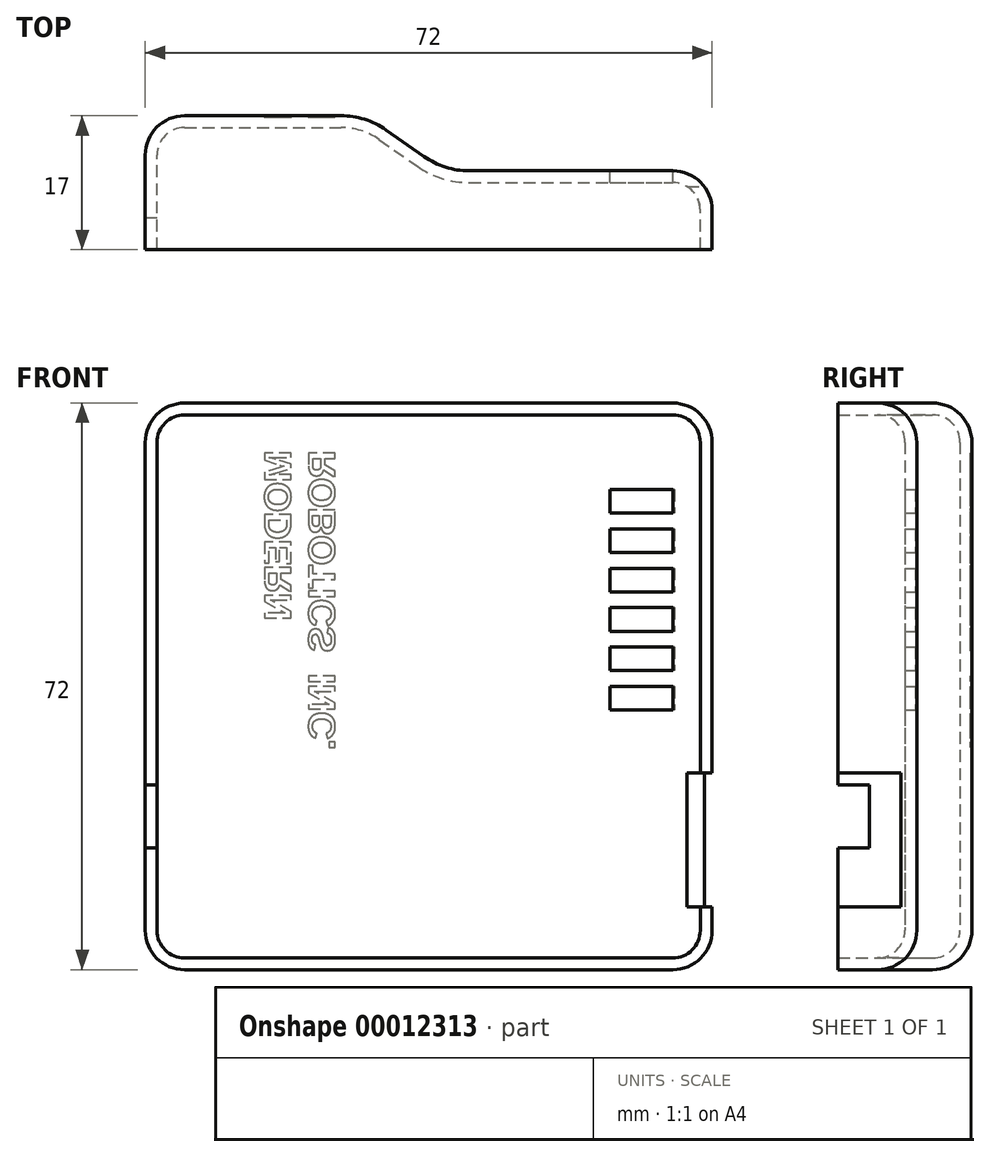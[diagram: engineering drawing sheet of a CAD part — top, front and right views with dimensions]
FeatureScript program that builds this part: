
annotation { "Feature Type Name" : "Feature", "Feature Type Description" : "" }
export const myFeature = defineFeature(function(context is Context, id is Id, definition is map)
    precondition{}
    {
        {
            var Q0;
            Q0=qCreatedBy(makeId("Top.planeOp"),FACE);
            var sketch = newSketch(context, id + "F0", { "sketchPlane" : qUnion([Q0])});
            skPoint(sketch, "E0.visualSharp", {"position": v(28, 17) * mm});
            skPoint(sketch, "E1.visualSharp", {"position": v(38, 10) * mm});
            skLineSegment(sketch, "E2", {"start": v(0, 0) * mm, "end": v(72, 0) * mm});
            skLineSegment(sketch, "E3", {"start": v(72, 10) * mm, "end": v(41.15, 10) * mm});
            skLineSegment(sketch, "E4", {"start": v(72, 0) * mm, "end": v(72, 10) * mm});
            skLineSegment(sketch, "E5", {"start": v(24.85, 17) * mm, "end": v(0, 17) * mm});
            skLineSegment(sketch, "E6", {"start": v(35.42, 11.8) * mm, "end": v(30.58, 15.2) * mm});
            skArc(sketch, "E0.filletArc", {"start": v(30.58, 15.2) * mm, "mid": v(27.85, 16.54) * mm, "end": v(24.85, 17) * mm});
            skLineSegment(sketch, "E7", {"start": v(0, 17) * mm, "end": v(0, 0) * mm});
            skArc(sketch, "E1.filletArc", {"start": v(35.42, 11.8) * mm, "mid": v(38.15, 10.46) * mm, "end": v(41.15, 10) * mm});
            skSolve(sketch);
        }
        {
            var Q0;
            Q0=qSketchRegion(id+"F0",true);
            extrude(context, id + "F1", {"entities" : qUnion([Q0]), "depth" : 72 * mm});
        }
        {
            var Q0;
            Q0=makeQuery(id+"F1.opExtrude","CAP_EDGE",EDGE,{"disambiguationData":[OSD([sQuery(id+"F0.wireOp",EDGE,"E5")])],"isStart":false});
            var Q1;
            Q1=makeQuery(id+"F1.opExtrude","SWEPT_EDGE",EDGE,{"disambiguationData":[OSD([sQuery(id+"F0.wireOp",EDGE,"E3"),sQuery(id+"F0.wireOp",EDGE,"E4")])]});
            var Q2;
            Q2=makeQuery(id+"F1.opExtrude","CAP_EDGE",EDGE,{"disambiguationData":[OSD([sQuery(id+"F0.wireOp",EDGE,"E3")])],"isStart":true});
            var Q3;
            Q3=makeQuery(id+"F1.opExtrude","SWEPT_EDGE",EDGE,{"disambiguationData":[OSD([sQuery(id+"F0.wireOp",EDGE,"E5"),sQuery(id+"F0.wireOp",EDGE,"E7")])]});
            var Q4;
            Q4=makeQuery(id+"F1.opExtrude","CAP_EDGE",EDGE,{"disambiguationData":[OSD([sQuery(id+"F0.wireOp",EDGE,"E7")])],"isStart":false});
            var Q5;
            Q5=makeQuery(id+"F1.opExtrude","CAP_EDGE",EDGE,{"disambiguationData":[OSD([sQuery(id+"F0.wireOp",EDGE,"E4")])],"isStart":false});
            var Q6;
            Q6=makeQuery(id+"F1.opExtrude","CAP_EDGE",EDGE,{"disambiguationData":[OSD([sQuery(id+"F0.wireOp",EDGE,"E4")])],"isStart":true});
            var Q7;
            Q7=makeQuery(id+"F1.opExtrude","CAP_EDGE",EDGE,{"disambiguationData":[OSD([sQuery(id+"F0.wireOp",EDGE,"E7")])],"isStart":true});
            fillet(context, id + "F2", {"entities" : qUnion([Q0, Q1, Q2, Q3, Q4, Q5, Q6, Q7]), "radius" : 5 * mm, "tangentPropagation" : true, "allowEdgeOverflow" : false});
        }
        {
            var Q0;
            Q0=makeQuery(id+"F1.opExtrude","SWEPT_FACE",FACE,{"disambiguationData":[OSD([sQuery(id+"F0.wireOp",EDGE,"E2")])]});
            var Q1;
            Q1=makeQuery(id+"F1.opExtrude","SWEPT_BODY",BODY,{"disambiguationData":[OSD([sQuery(id+"F0.wireOp",EDGE,"E2"),sQuery(id+"F0.wireOp",EDGE,"E3"),sQuery(id+"F0.wireOp",EDGE,"E4"),sQuery(id+"F0.wireOp",EDGE,"E5"),sQuery(id+"F0.wireOp",EDGE,"E6"),sQuery(id+"F0.wireOp",EDGE,"E0.filletArc"),sQuery(id+"F0.wireOp",EDGE,"E7"),sQuery(id+"F0.wireOp",EDGE,"E1.filletArc")])]});
            shell(context, id + "F3", {"entities" : qUnion([Q0]), "parts" : qUnion([Q1]), "thickness" : 1.5 * mm});
        }
        {
            var Q0;
            Q0=makeQuery(id+"F1.opExtrude","SWEPT_FACE",FACE,{"disambiguationData":[OSD([sQuery(id+"F0.wireOp",EDGE,"E7")])]});
            var sketch = newSketch(context, id + "F4", { "sketchPlane" : qUnion([Q0])});
            skLineSegment(sketch, "E8.bottom", {"start": v(0, 23.5) * mm, "end": v(-4, 23.5) * mm});
            skLineSegment(sketch, "E8.top", {"start": v(0, 15.5) * mm, "end": v(-4, 15.5) * mm});
            skLineSegment(sketch, "E8.left", {"start": v(0, 23.5) * mm, "end": v(0, 15.5) * mm});
            skLineSegment(sketch, "E8.right", {"start": v(-4, 23.5) * mm, "end": v(-4, 15.5) * mm});
            skSolve(sketch);
        }
        {
            var Q0;
            Q0=qSketchRegion(id+"F4",true);
            extrude(context, id + "F5", {"entities" : qUnion([Q0]), "operationType" : NewBodyOperationType.REMOVE, "endBound" : BoundingType.UP_TO_NEXT, "oppositeDirection" : true, "depth" : 25 * mm});
        }
        {
            var Q0;
            Q0=makeQuery(id+"F1.opExtrude","SWEPT_FACE",FACE,{"disambiguationData":[OSD([sQuery(id+"F0.wireOp",EDGE,"E5")])]});
            var sketch = newSketch(context, id + "F6", { "sketchPlane" : qUnion([Q0])});
            skText(sketch, "E9", { "text": "MODERN\nROBOTICS  INC.", "fontName": "Arimo-Bold.ttf"});
            const initialGuessF6  = {"E9": [-0.0185, 0.066, 0, -1, 0.0035]};
            skSetInitialGuess(sketch, initialGuessF6);
            skSolve(sketch);
        }
        {
            var Q0;
            Q0=qSketchRegion(id+"F6",true);
            extrude(context, id + "F7", {"entities" : qUnion([Q0]), "operationType" : NewBodyOperationType.REMOVE, "oppositeDirection" : true, "depth" : .2 * mm});
        }
        {
            var Q0;
            Q0=makeQuery(id+"F1.opExtrude","SWEPT_FACE",FACE,{"disambiguationData":[OSD([sQuery(id+"F0.wireOp",EDGE,"E3")])]});
            var sketch = newSketch(context, id + "F8", { "sketchPlane" : qUnion([Q0])});
            skLineSegment(sketch, "E10.bottom", {"start": v(-59, 61) * mm, "end": v(-67, 61) * mm});
            skLineSegment(sketch, "E10.top", {"start": v(-59, 58) * mm, "end": v(-67, 58) * mm});
            skLineSegment(sketch, "E10.left", {"start": v(-59, 61) * mm, "end": v(-59, 58) * mm});
            skLineSegment(sketch, "E10.right", {"start": v(-67, 61) * mm, "end": v(-67, 58) * mm});
            skLineSegment(sketch, "E11.0.1.0", {"start": v(-59, 56) * mm, "end": v(-67, 56) * mm});
            skLineSegment(sketch, "E11.0.1.1", {"start": v(-59, 53) * mm, "end": v(-67, 53) * mm});
            skLineSegment(sketch, "E11.0.1.2", {"start": v(-59, 56) * mm, "end": v(-59, 53) * mm});
            skLineSegment(sketch, "E11.0.1.3", {"start": v(-67, 56) * mm, "end": v(-67, 53) * mm});
            skLineSegment(sketch, "E11.0.2.0", {"start": v(-59, 51) * mm, "end": v(-67, 51) * mm});
            skLineSegment(sketch, "E11.0.2.1", {"start": v(-59, 48) * mm, "end": v(-67, 48) * mm});
            skLineSegment(sketch, "E11.0.2.2", {"start": v(-59, 51) * mm, "end": v(-59, 48) * mm});
            skLineSegment(sketch, "E11.0.2.3", {"start": v(-67, 51) * mm, "end": v(-67, 48) * mm});
            skLineSegment(sketch, "E11.0.3.0", {"start": v(-59, 46) * mm, "end": v(-67, 46) * mm});
            skLineSegment(sketch, "E11.0.3.1", {"start": v(-59, 43) * mm, "end": v(-67, 43) * mm});
            skLineSegment(sketch, "E11.0.3.2", {"start": v(-59, 46) * mm, "end": v(-59, 43) * mm});
            skLineSegment(sketch, "E11.0.3.3", {"start": v(-67, 46) * mm, "end": v(-67, 43) * mm});
            skLineSegment(sketch, "E11.0.4.0", {"start": v(-59, 41) * mm, "end": v(-67, 41) * mm});
            skLineSegment(sketch, "E11.0.4.1", {"start": v(-59, 38) * mm, "end": v(-67, 38) * mm});
            skLineSegment(sketch, "E11.0.4.2", {"start": v(-59, 41) * mm, "end": v(-59, 38) * mm});
            skLineSegment(sketch, "E11.0.4.3", {"start": v(-67, 41) * mm, "end": v(-67, 38) * mm});
            skLineSegment(sketch, "E11.0.5.0", {"start": v(-59, 36) * mm, "end": v(-67, 36) * mm});
            skLineSegment(sketch, "E11.0.5.1", {"start": v(-59, 33) * mm, "end": v(-67, 33) * mm});
            skLineSegment(sketch, "E11.0.5.2", {"start": v(-59, 36) * mm, "end": v(-59, 33) * mm});
            skLineSegment(sketch, "E11.0.5.3", {"start": v(-67, 36) * mm, "end": v(-67, 33) * mm});
            skLineSegment(sketch, "E11.direction1", {"start": v(-67, 61) * mm, "end": v(-42, 61) * mm, "construction": true});
            skLineSegment(sketch, "E11.direction2", {"start": v(-67, 61) * mm, "end": v(-67, 56) * mm, "construction": true});
            skSolve(sketch);
        }
        {
            var Q0;
            Q0=qSketchRegion(id+"F8",true);
            extrude(context, id + "F9", {"entities" : qUnion([Q0]), "operationType" : NewBodyOperationType.REMOVE, "endBound" : BoundingType.UP_TO_NEXT, "oppositeDirection" : true, "depth" : 25 * mm});
        }
        {
            var Q0;
            {var subQ0=sQuery(id+"F0.wireOp",EDGE,"E3");Q0=makeQuery(id+"F9.boolean.opBoolean","MERGE",EDGE,{"derivedFrom":[makeQuery(id+"F2.opFillet","BLEND_EDGE",EDGE,{"blendedFrom":[makeQuery(id+"F1.opExtrude","SWEPT_EDGE",EDGE,{"disambiguationData":[OSD([subQ0,sQuery(id+"F0.wireOp",EDGE,"E4")])]}),makeQuery(id+"F1.opExtrude","SWEPT_FACE",FACE,{"disambiguationData":[OSD([subQ0])]})],"blendedInto":[makeQuery(id+"F1.opExtrude","SWEPT_FACE",FACE,{"disambiguationData":[OSD([subQ0])]})]}),makeQuery(id+"F9.opExtrude","CAP_EDGE",EDGE,{"disambiguationData":[OSD([sQuery(id+"F8.wireOp",EDGE,"E10.right")])],"isStart":true})]});}
            var Q1;
            Q1=makeQuery(id+"F9.boolean.opBoolean","COPY",EDGE,{"derivedFrom":makeQuery(id+"F9.opExtrude","CAP_EDGE",EDGE,{"disambiguationData":[OSD([sQuery(id+"F8.wireOp",EDGE,"E10.bottom")])],"isStart":true})});
            var Q2;
            Q2=makeQuery(id+"F9.boolean.opBoolean","COPY",EDGE,{"derivedFrom":makeQuery(id+"F9.opExtrude","CAP_EDGE",EDGE,{"disambiguationData":[OSD([sQuery(id+"F8.wireOp",EDGE,"E10.left")])],"isStart":true})});
            var Q3;
            Q3=makeQuery(id+"F9.boolean.opBoolean","COPY",EDGE,{"derivedFrom":makeQuery(id+"F9.opExtrude","CAP_EDGE",EDGE,{"disambiguationData":[OSD([sQuery(id+"F8.wireOp",EDGE,"E10.top")])],"isStart":true})});
            var Q4;
            Q4=makeQuery(id+"F9.boolean.opBoolean","COPY",EDGE,{"derivedFrom":makeQuery(id+"F9.opExtrude","CAP_EDGE",EDGE,{"disambiguationData":[OSD([sQuery(id+"F8.wireOp",EDGE,"E11.0.1.0")])],"isStart":true})});
            var Q5;
            {var subQ0=sQuery(id+"F0.wireOp",EDGE,"E3");Q5=makeQuery(id+"F9.boolean.opBoolean","MERGE",EDGE,{"derivedFrom":[makeQuery(id+"F2.opFillet","BLEND_EDGE",EDGE,{"blendedFrom":[makeQuery(id+"F1.opExtrude","SWEPT_EDGE",EDGE,{"disambiguationData":[OSD([subQ0,sQuery(id+"F0.wireOp",EDGE,"E4")])]}),makeQuery(id+"F1.opExtrude","SWEPT_FACE",FACE,{"disambiguationData":[OSD([subQ0])]})],"blendedInto":[makeQuery(id+"F1.opExtrude","SWEPT_FACE",FACE,{"disambiguationData":[OSD([subQ0])]})]}),makeQuery(id+"F9.opExtrude","CAP_EDGE",EDGE,{"disambiguationData":[OSD([sQuery(id+"F8.wireOp",EDGE,"E11.0.1.3")])],"isStart":true})]});}
            var Q6;
            Q6=makeQuery(id+"F9.boolean.opBoolean","COPY",EDGE,{"derivedFrom":makeQuery(id+"F9.opExtrude","CAP_EDGE",EDGE,{"disambiguationData":[OSD([sQuery(id+"F8.wireOp",EDGE,"E11.0.1.2")])],"isStart":true})});
            var Q7;
            Q7=makeQuery(id+"F9.boolean.opBoolean","COPY",EDGE,{"derivedFrom":makeQuery(id+"F9.opExtrude","CAP_EDGE",EDGE,{"disambiguationData":[OSD([sQuery(id+"F8.wireOp",EDGE,"E11.0.1.1")])],"isStart":true})});
            var Q8;
            Q8=makeQuery(id+"F9.boolean.opBoolean","COPY",EDGE,{"derivedFrom":makeQuery(id+"F9.opExtrude","CAP_EDGE",EDGE,{"disambiguationData":[OSD([sQuery(id+"F8.wireOp",EDGE,"E11.0.2.2")])],"isStart":true})});
            var Q9;
            Q9=makeQuery(id+"F9.boolean.opBoolean","COPY",EDGE,{"derivedFrom":makeQuery(id+"F9.opExtrude","CAP_EDGE",EDGE,{"disambiguationData":[OSD([sQuery(id+"F8.wireOp",EDGE,"E11.0.2.0")])],"isStart":true})});
            var Q10;
            {var subQ0=sQuery(id+"F0.wireOp",EDGE,"E3");Q10=makeQuery(id+"F9.boolean.opBoolean","MERGE",EDGE,{"derivedFrom":[makeQuery(id+"F2.opFillet","BLEND_EDGE",EDGE,{"blendedFrom":[makeQuery(id+"F1.opExtrude","SWEPT_EDGE",EDGE,{"disambiguationData":[OSD([subQ0,sQuery(id+"F0.wireOp",EDGE,"E4")])]}),makeQuery(id+"F1.opExtrude","SWEPT_FACE",FACE,{"disambiguationData":[OSD([subQ0])]})],"blendedInto":[makeQuery(id+"F1.opExtrude","SWEPT_FACE",FACE,{"disambiguationData":[OSD([subQ0])]})]}),makeQuery(id+"F9.opExtrude","CAP_EDGE",EDGE,{"disambiguationData":[OSD([sQuery(id+"F8.wireOp",EDGE,"E11.0.2.3")])],"isStart":true})]});}
            var Q11;
            Q11=makeQuery(id+"F9.boolean.opBoolean","COPY",EDGE,{"derivedFrom":makeQuery(id+"F9.opExtrude","CAP_EDGE",EDGE,{"disambiguationData":[OSD([sQuery(id+"F8.wireOp",EDGE,"E11.0.2.1")])],"isStart":true})});
            var Q12;
            Q12=makeQuery(id+"F9.boolean.opBoolean","COPY",EDGE,{"derivedFrom":makeQuery(id+"F9.opExtrude","CAP_EDGE",EDGE,{"disambiguationData":[OSD([sQuery(id+"F8.wireOp",EDGE,"E11.0.3.1")])],"isStart":true})});
            var Q13;
            {var subQ0=sQuery(id+"F0.wireOp",EDGE,"E3");Q13=makeQuery(id+"F9.boolean.opBoolean","MERGE",EDGE,{"derivedFrom":[makeQuery(id+"F2.opFillet","BLEND_EDGE",EDGE,{"blendedFrom":[makeQuery(id+"F1.opExtrude","SWEPT_EDGE",EDGE,{"disambiguationData":[OSD([subQ0,sQuery(id+"F0.wireOp",EDGE,"E4")])]}),makeQuery(id+"F1.opExtrude","SWEPT_FACE",FACE,{"disambiguationData":[OSD([subQ0])]})],"blendedInto":[makeQuery(id+"F1.opExtrude","SWEPT_FACE",FACE,{"disambiguationData":[OSD([subQ0])]})]}),makeQuery(id+"F9.opExtrude","CAP_EDGE",EDGE,{"disambiguationData":[OSD([sQuery(id+"F8.wireOp",EDGE,"E11.0.3.3")])],"isStart":true})]});}
            var Q14;
            Q14=makeQuery(id+"F9.boolean.opBoolean","COPY",EDGE,{"derivedFrom":makeQuery(id+"F9.opExtrude","CAP_EDGE",EDGE,{"disambiguationData":[OSD([sQuery(id+"F8.wireOp",EDGE,"E11.0.3.0")])],"isStart":true})});
            var Q15;
            Q15=makeQuery(id+"F9.boolean.opBoolean","COPY",EDGE,{"derivedFrom":makeQuery(id+"F9.opExtrude","CAP_EDGE",EDGE,{"disambiguationData":[OSD([sQuery(id+"F8.wireOp",EDGE,"E11.0.3.2")])],"isStart":true})});
            var Q16;
            Q16=makeQuery(id+"F9.boolean.opBoolean","COPY",EDGE,{"derivedFrom":makeQuery(id+"F9.opExtrude","CAP_EDGE",EDGE,{"disambiguationData":[OSD([sQuery(id+"F8.wireOp",EDGE,"E11.0.4.2")])],"isStart":true})});
            var Q17;
            Q17=makeQuery(id+"F9.boolean.opBoolean","COPY",EDGE,{"derivedFrom":makeQuery(id+"F9.opExtrude","CAP_EDGE",EDGE,{"disambiguationData":[OSD([sQuery(id+"F8.wireOp",EDGE,"E11.0.4.0")])],"isStart":true})});
            var Q18;
            {var subQ0=sQuery(id+"F0.wireOp",EDGE,"E3");Q18=makeQuery(id+"F9.boolean.opBoolean","MERGE",EDGE,{"derivedFrom":[makeQuery(id+"F2.opFillet","BLEND_EDGE",EDGE,{"blendedFrom":[makeQuery(id+"F1.opExtrude","SWEPT_EDGE",EDGE,{"disambiguationData":[OSD([subQ0,sQuery(id+"F0.wireOp",EDGE,"E4")])]}),makeQuery(id+"F1.opExtrude","SWEPT_FACE",FACE,{"disambiguationData":[OSD([subQ0])]})],"blendedInto":[makeQuery(id+"F1.opExtrude","SWEPT_FACE",FACE,{"disambiguationData":[OSD([subQ0])]})]}),makeQuery(id+"F9.opExtrude","CAP_EDGE",EDGE,{"disambiguationData":[OSD([sQuery(id+"F8.wireOp",EDGE,"E11.0.4.3")])],"isStart":true})]});}
            var Q19;
            Q19=makeQuery(id+"F9.boolean.opBoolean","COPY",EDGE,{"derivedFrom":makeQuery(id+"F9.opExtrude","CAP_EDGE",EDGE,{"disambiguationData":[OSD([sQuery(id+"F8.wireOp",EDGE,"E11.0.4.1")])],"isStart":true})});
            var Q20;
            Q20=makeQuery(id+"F9.boolean.opBoolean","COPY",EDGE,{"derivedFrom":makeQuery(id+"F9.opExtrude","CAP_EDGE",EDGE,{"disambiguationData":[OSD([sQuery(id+"F8.wireOp",EDGE,"E11.0.5.2")])],"isStart":true})});
            var Q21;
            {var subQ0=sQuery(id+"F0.wireOp",EDGE,"E3");Q21=makeQuery(id+"F9.boolean.opBoolean","MERGE",EDGE,{"derivedFrom":[makeQuery(id+"F2.opFillet","BLEND_EDGE",EDGE,{"blendedFrom":[makeQuery(id+"F1.opExtrude","SWEPT_EDGE",EDGE,{"disambiguationData":[OSD([subQ0,sQuery(id+"F0.wireOp",EDGE,"E4")])]}),makeQuery(id+"F1.opExtrude","SWEPT_FACE",FACE,{"disambiguationData":[OSD([subQ0])]})],"blendedInto":[makeQuery(id+"F1.opExtrude","SWEPT_FACE",FACE,{"disambiguationData":[OSD([subQ0])]})]}),makeQuery(id+"F9.opExtrude","CAP_EDGE",EDGE,{"disambiguationData":[OSD([sQuery(id+"F8.wireOp",EDGE,"E11.0.5.3")])],"isStart":true})]});}
            var Q22;
            Q22=makeQuery(id+"F9.boolean.opBoolean","COPY",EDGE,{"derivedFrom":makeQuery(id+"F9.opExtrude","CAP_EDGE",EDGE,{"disambiguationData":[OSD([sQuery(id+"F8.wireOp",EDGE,"E11.0.5.0")])],"isStart":true})});
            var Q23;
            Q23=makeQuery(id+"F9.boolean.opBoolean","COPY",EDGE,{"derivedFrom":makeQuery(id+"F9.opExtrude","CAP_EDGE",EDGE,{"disambiguationData":[OSD([sQuery(id+"F8.wireOp",EDGE,"E11.0.5.1")])],"isStart":true})});
            chamfer(context, id + "F10", {"entities" : qUnion([Q0, Q1, Q2, Q3, Q4, Q5, Q6, Q7, Q8, Q9, Q10, Q11, Q12, Q13, Q14, Q15, Q16, Q17, Q18, Q19, Q20, Q21, Q22, Q23]), "width" : .2 * mm, "tangentPropagation" : true});
        }
        {
            var Q0;
            Q0=makeQuery(id+"F1.opExtrude","SWEPT_FACE",FACE,{"disambiguationData":[OSD([sQuery(id+"F0.wireOp",EDGE,"E4")])]});
            var sketch = newSketch(context, id + "F11", { "sketchPlane" : qUnion([Q0])});
            skLineSegment(sketch, "E12.bottom", {"start": v(0, 25) * mm, "end": v(8, 25) * mm});
            skLineSegment(sketch, "E12.left", {"start": v(0, 25) * mm, "end": v(0, 8) * mm});
            skLineSegment(sketch, "E12.right", {"start": v(8, 25) * mm, "end": v(8, 8) * mm});
            skLineSegment(sketch, "E12.top", {"start": v(0, 8) * mm, "end": v(8, 8) * mm});
            skSolve(sketch);
        }
        {
            var Q0;
            Q0=qSketchRegion(id+"F11",true);
            extrude(context, id + "F12", {"entities" : qUnion([Q0]), "operationType" : NewBodyOperationType.REMOVE, "endBound" : BoundingType.UP_TO_NEXT, "oppositeDirection" : true, "depth" : 25 * mm});
        }
    });
